# Revit family: oventrop_hydromat-qtr_1061604-12rfa
name_source: partatom
category: Арматура трубопроводов
revit_build: Autodesk Revit 2017 (Build: 20160225_1515(x64)
units: mm (PartAtom-declared; Revit-internal decimal feet)

## family parameters
Всегда вертикально = Да
Заголовок OmniClass = Adjusting/Controlling Valves for Liquid Services
На основе рабочей плоскости = Нет
Номер OmniClass = 23.65.55.14.17
Общий = Нет
При загрузке вырезать с полостями = Нет
Размер круглого соединителя = Использовать радиус
Тип детали = Клапан - Вставляется

## types (5) — shared parameters
Angle = 50.00°
Article Description = Proportional flow regulators with male ports
Article Type = Hydromat QTR 10616
Bonnet = Color RGB 35-35-35
Bronze = Color RGB 156-122-90
Custom = Нет
D_Bonnet = 114 мм
EMCS Version = 2.0
ETIM Article Class = EC011435
Family Version = 10.14
Hb4 = 18 мм
Hb5 = 3 мм
Hlp1 = 22 мм
IFCExportAs = IfcValveType
IFCExportType = REGULATING
Lgt2 = 11 мм
MEPcontent Class = VALVE_CONTROL
Manufacturer URL = http://www.oventrop.de
Pressure Drop = 0.0 Па
Product Line = Oventrop
R1_Bonnet = 25 мм
R2_Bonnet = 34 мм
Rcut_Bonnet = 24 мм
Revit Version = 2015
r1 = 2 мм
r2 = 3 мм
r3_Bonnet = 16 мм
Группа модели = Hydromat QTR 10616
Изготовитель = Oventrop
Описание = Proportional flow regulators with male ports

## per-type parameters (varying)
- DN 40: Female_Port_Width=13 мм; GTIN=4026755125801; H1_Bonnet=37 мм; H_Bonnet=153 мм; Hb1=142 мм; Hb2=19 мм; Hb3=15 мм; Hb6=46 мм; Height=131 мм; L2=5 мм; Length=88 мм; Lgt1=15 мм; Manufacturer Art. No.=1061604; NominalDiameter=15 мм; Nut_Dimension_In=27 мм; Nut_Dimension_Out=30 мм; OuterDiameter=21 мм; Rad1=11 мм; Rad2=11 мм; Rad3=13 мм; Rad4=16 мм; Rad5=18 мм; SW_In=31 мм; SW_Out=35 мм; URL=www.stabiplan.com
- DN 32: Female_Port_Width=19 мм; GTIN=4026755125832; H1_Bonnet=38 мм; H_Bonnet=159 мм; Hb1=160 мм; Hb2=50 мм; Hb3=1 мм; Hb6=64 мм; Height=145 мм; L2=10 мм; Length=110 мм; Lgt1=21 мм; Manufacturer Art. No.=1061610; NominalDiameter=32 мм; Nut_Dimension_In=50 мм; Nut_Dimension_Out=52 мм; OuterDiameter=42 мм; Rad1=21 мм; Rad2=21 мм; Rad3=24 мм; Rad4=26 мм; Rad5=28 мм; SW_In=58 мм; SW_Out=60 мм; URL=www.stabiplan.com
- DN 25: Female_Port_Width=17 мм; GTIN=4026755125825; H1_Bonnet=42 мм; H_Bonnet=173 мм; Hb1=148 мм; Hb2=25 мм; Hb3=13 мм; Hb6=49 мм; Height=136 мм; L2=8 мм; Length=110 мм; Lgt1=19 мм; Manufacturer Art. No.=1061608; NominalDiameter=25 мм; Nut_Dimension_In=41 мм; Nut_Dimension_Out=46 мм; OuterDiameter=34 мм; Rad1=17 мм; Rad2=17 мм; Rad3=19 мм; Rad4=22 мм; Rad5=24 мм; SW_In=47 мм; SW_Out=53 мм; URL=www.stabiplan.com
- DN 20: Female_Port_Width=15 мм; GTIN=4026755125818; H1_Bonnet=44 мм; H_Bonnet=184 мм; Hb1=144 мм; Hb2=22 мм; Hb3=11 мм; Hb6=44 мм; Height=133 мм; L2=6 мм; Length=93 мм; Lgt1=17 мм; Manufacturer Art. No.=1061606; NominalDiameter=20 мм; Nut_Dimension_In=32 мм; Nut_Dimension_Out=37 мм; OuterDiameter=27 мм; Rad1=13 мм; Rad2=13 мм; Rad3=16 мм; Rad4=18 мм; Rad5=20 мм; SW_In=37 мм; SW_Out=43 мм; URL=www.stabiplan.com
- DN 15: Female_Port_Width=13 мм; GTIN=4026755125801; H1_Bonnet=37 мм; H_Bonnet=153 мм; Hb1=142 мм; Hb2=19 мм; Hb3=15 мм; Hb6=46 мм; Height=131 мм; L2=5 мм; Length=88 мм; Lgt1=15 мм; Manufacturer Art. No.=1061604; NominalDiameter=15 мм; Nut_Dimension_In=27 мм; Nut_Dimension_Out=30 мм; OuterDiameter=21 мм; Rad1=11 мм; Rad2=11 мм; Rad3=13 мм; Rad4=16 мм; Rad5=18 мм; SW_In=31 мм; SW_Out=35 мм; URL=http://file-system.ru

## geometry (parser evidence)
native form markers: Sweep x2
no freeform markers — native parametric forms only
